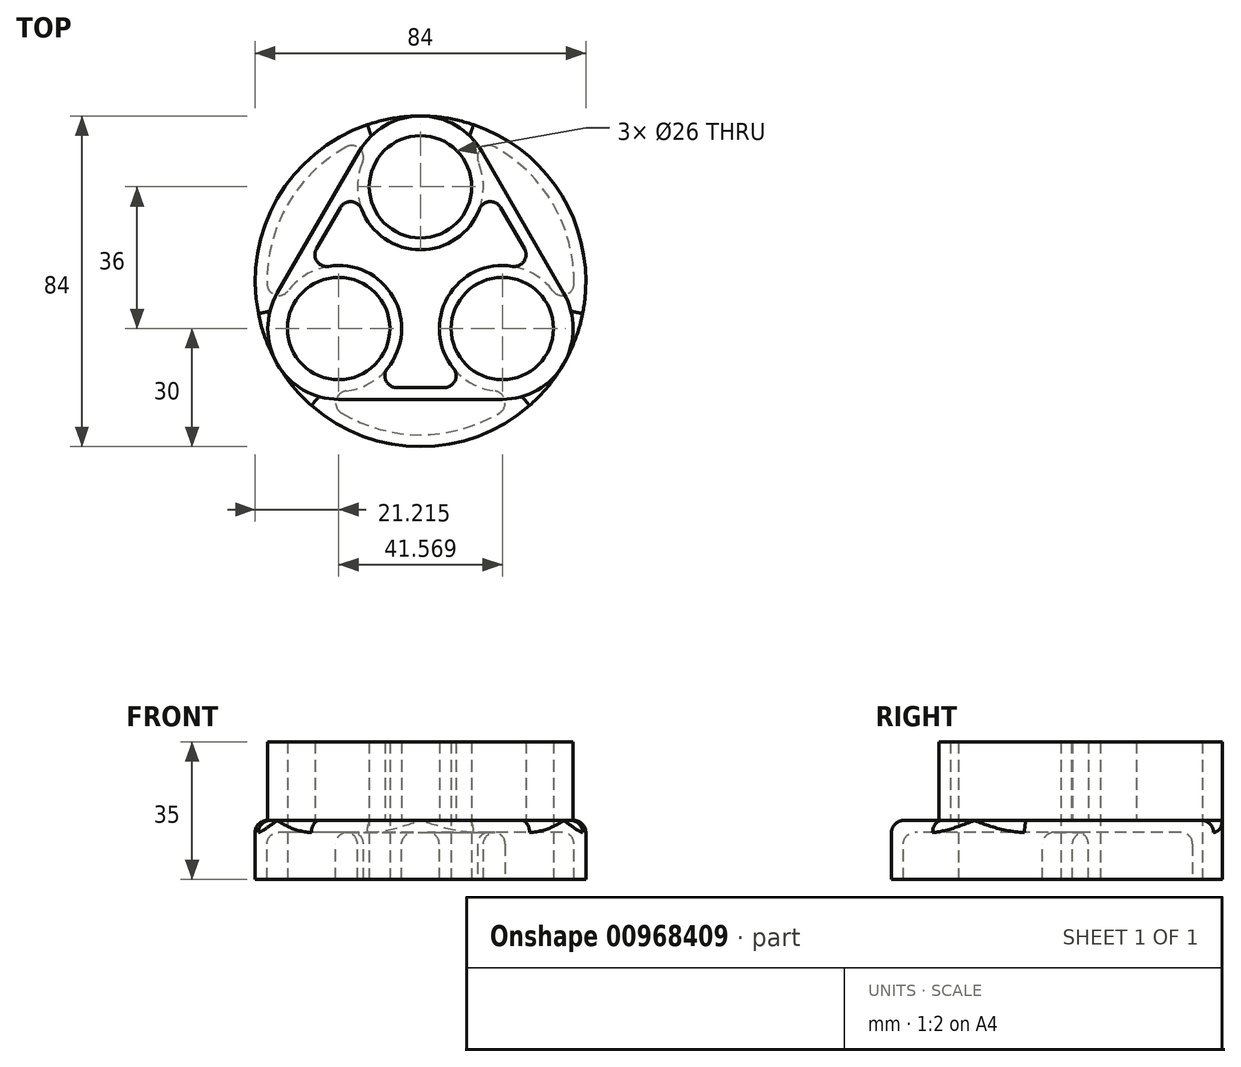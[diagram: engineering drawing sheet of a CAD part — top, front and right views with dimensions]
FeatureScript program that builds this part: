
annotation { "Feature Type Name" : "Feature", "Feature Type Description" : "" }
export const myFeature = defineFeature(function(context is Context, id is Id, definition is map)
    precondition{}
    {
        {
            var Q0;
            Q0=qCreatedBy(makeId("Top.planeOp"),FACE);
            var sketch = newSketch(context, id + "F0", { "sketchPlane" : qUnion([Q0])});
            skCircle(sketch, "E0", {"center": v(0, 0) * mm, "radius": 42 * mm, "construction": true});
            skCircle(sketch, "E1", {"center": v(0, 24) * mm, "radius": 13 * mm});
            skLineSegment(sketch, "E2", {"start": v(0, 0) * mm, "end": v(-20.78, -12) * mm, "construction": true});
            skLineSegment(sketch, "E3", {"start": v(0, 0) * mm, "end": v(20.78, -12) * mm, "construction": true});
            skCircle(sketch, "E4", {"center": v(-20.78, -12) * mm, "radius": 13 * mm});
            skCircle(sketch, "E5", {"center": v(20.78, -12) * mm, "radius": 13 * mm});
            skCircle(sketch, "E6", {"center": v(0, 0) * mm, "radius": 24 * mm, "construction": true});
            skArc(sketch, "E7", {"start": v(-15.59, 33) * mm, "mid": v(0, 42) * mm, "end": v(15.59, 33) * mm});
            skArc(sketch, "E8", {"start": v(-36.37, -3) * mm, "mid": v(-36.37, -21) * mm, "end": v(-20.78, -30) * mm});
            skArc(sketch, "E9", {"start": v(36.37, -3) * mm, "mid": v(36.37, -21) * mm, "end": v(20.78, -30) * mm});
            skLineSegment(sketch, "E10", {"start": v(-15.59, 33) * mm, "end": v(-36.37, -3) * mm});
            skLineSegment(sketch, "E11", {"start": v(15.59, 33) * mm, "end": v(36.37, -3) * mm});
            skLineSegment(sketch, "E12", {"start": v(-20.78, -30) * mm, "end": v(20.78, -30) * mm});
            skArc(sketch, "E13", {"start": v(-14.95, 18.3) * mm, "mid": v(0, 8) * mm, "end": v(14.95, 18.3) * mm});
            skArc(sketch, "E14", {"start": v(8.38, -22.1) * mm, "mid": v(6.93, -4) * mm, "end": v(23.33, 3.8) * mm});
            skArc(sketch, "E15", {"start": v(-23.33, 3.8) * mm, "mid": v(-6.93, -4) * mm, "end": v(-8.38, -22.1) * mm});
            skLineSegment(sketch, "E16", {"start": v(-6.05, -27) * mm, "end": v(6.05, -27) * mm});
            skLineSegment(sketch, "E17", {"start": v(20.36, 18.74) * mm, "end": v(26.4, 8.26) * mm});
            skLineSegment(sketch, "E18.0", {"start": v(-20.36, 18.74) * mm, "end": v(-26.4, 8.26) * mm});
            skPoint(sketch, "E19.visualSharp", {"position": v(-15.77, 26.68) * mm});
            skArc(sketch, "E19.filletArc", {"start": v(-14.95, 18.3) * mm, "mid": v(-17.52, 20.23) * mm, "end": v(-20.36, 18.74) * mm});
            skPoint(sketch, "E20.visualSharp", {"position": v(15.77, 26.68) * mm});
            skArc(sketch, "E20.filletArc", {"start": v(20.36, 18.74) * mm, "mid": v(17.52, 20.23) * mm, "end": v(14.95, 18.3) * mm});
            skPoint(sketch, "E21.visualSharp", {"position": v(31, 0.32) * mm});
            skArc(sketch, "E21.filletArc", {"start": v(23.33, 3.8) * mm, "mid": v(26.28, 5.05) * mm, "end": v(26.4, 8.26) * mm});
            skPoint(sketch, "E22.visualSharp", {"position": v(-31, 0.32) * mm});
            skArc(sketch, "E22.filletArc", {"start": v(-26.4, 8.26) * mm, "mid": v(-26.28, 5.05) * mm, "end": v(-23.33, 3.8) * mm});
            skPoint(sketch, "E23.visualSharp", {"position": v(15.22, -27) * mm});
            skArc(sketch, "E23.filletArc", {"start": v(6.05, -27) * mm, "mid": v(8.76, -25.29) * mm, "end": v(8.38, -22.1) * mm});
            skPoint(sketch, "E24.visualSharp", {"position": v(-15.22, -27) * mm});
            skArc(sketch, "E24.filletArc", {"start": v(-8.38, -22.1) * mm, "mid": v(-8.76, -25.29) * mm, "end": v(-6.05, -27) * mm});
            skSolve(sketch);
        }
        {
            var Q0;
            Q0=qCreatedBy(makeId("Top.planeOp"),FACE);
            var sketch = newSketch(context, id + "F1", { "sketchPlane" : qUnion([Q0])});
            skCircle(sketch, "E25.0", {"center": v(0, 0) * mm, "radius": 42 * mm});
            skCircle(sketch, "E26.0", {"center": v(0, 24) * mm, "radius": 13 * mm});
            skCircle(sketch, "E26.1", {"center": v(20.78, -12) * mm, "radius": 13 * mm});
            skCircle(sketch, "E26.2", {"center": v(-20.78, -12) * mm, "radius": 13 * mm});
            skCircle(sketch, "E27.0", {"center": v(0, 24) * mm, "radius": 16 * mm});
            skCircle(sketch, "E28.0", {"center": v(20.78, -12) * mm, "radius": 16 * mm});
            skCircle(sketch, "E29.0", {"center": v(-20.78, -12) * mm, "radius": 16 * mm});
            skSolve(sketch);
        }
        {
            var Q0;
            Q0=qSketchRegion(id+"F1",true);
            var Q1;
            Q1=makeQuery(id+"F1.imprint","IMPRINT",FACE,{"disambiguationData":[TD([[makeQuery(id+"F1.imprint","IMPRINT",EDGE,{"derivedFrom":sQuery(id+"F1.wireOp",EDGE,"E26.2")}),-1.0]])]});
            var Q2;
            Q2=makeQuery(id+"F1.imprint","IMPRINT",FACE,{"disambiguationData":[TD([[makeQuery(id+"F1.imprint","IMPRINT",EDGE,{"derivedFrom":sQuery(id+"F1.wireOp",EDGE,"E26.2")}),1.0]])]});
            var Q3;
            Q3=makeQuery(id+"F1.imprint","IMPRINT",FACE,{"disambiguationData":[TD([[makeQuery(id+"F1.imprint","IMPRINT",EDGE,{"derivedFrom":sQuery(id+"F1.wireOp",EDGE,"E26.0")}),-1.0]])]});
            var Q4;
            Q4=makeQuery(id+"F1.imprint","IMPRINT",FACE,{"disambiguationData":[TD([[makeQuery(id+"F1.imprint","IMPRINT",EDGE,{"derivedFrom":sQuery(id+"F1.wireOp",EDGE,"E26.0")}),1.0]])]});
            var Q5;
            Q5=makeQuery(id+"F1.imprint","IMPRINT",FACE,{"disambiguationData":[TD([[makeQuery(id+"F1.imprint","IMPRINT",EDGE,{"derivedFrom":sQuery(id+"F1.wireOp",EDGE,"E26.1")}),-1.0]])]});
            var Q6;
            Q6=makeQuery(id+"F1.imprint","IMPRINT",FACE,{"disambiguationData":[TD([[makeQuery(id+"F1.imprint","IMPRINT",EDGE,{"derivedFrom":sQuery(id+"F1.wireOp",EDGE,"E26.1")}),1.0]])]});
            extrude(context, id + "F2", {"entities" : qUnion([Q0, Q1, Q2, Q3, Q4, Q5, Q6]), "oppositeDirection" : true, "depth" : 15 * mm, "offsetDistance" : 25 * mm});
        }
        {
            var Q0;
            Q0=makeQuery(id+"F2.opExtrude","CAP_FACE",FACE,{"disambiguationData":[OSD([sQuery(id+"F1.wireOp",EDGE,"E25.0")])],"isStart":false});
            shell(context, id + "F3", {"entities" : qUnion([Q0]), "thickness" : 3 * mm});
        }
        {
            var Q0;
            Q0=makeQuery(id+"F0.imprint","IMPRINT",FACE,{"disambiguationData":[TD([[makeQuery(id+"F0.imprint","IMPRINT",EDGE,{"derivedFrom":sQuery(id+"F0.wireOp",EDGE,"E1")}),-1.0]])]});
            extrude(context, id + "F4", {"entities" : qUnion([Q0]), "operationType" : NewBodyOperationType.ADD, "depth" : 20 * mm, "offsetDistance" : 25 * mm});
        }
        {
            var Q0;
            Q0=makeQuery(id+"F0.imprint","IMPRINT",FACE,{"disambiguationData":[TD([[makeQuery(id+"F0.imprint","IMPRINT",EDGE,{"derivedFrom":sQuery(id+"F0.wireOp",EDGE,"E1")}),1.0]])]});
            var Q1;
            Q1=makeQuery(id+"F0.imprint","IMPRINT",FACE,{"disambiguationData":[TD([[makeQuery(id+"F0.imprint","IMPRINT",EDGE,{"derivedFrom":sQuery(id+"F0.wireOp",EDGE,"E4")}),1.0]])]});
            var Q2;
            Q2=makeQuery(id+"F0.imprint","IMPRINT",FACE,{"disambiguationData":[TD([[makeQuery(id+"F0.imprint","IMPRINT",EDGE,{"derivedFrom":sQuery(id+"F0.wireOp",EDGE,"E5")}),1.0]])]});
            extrude(context, id + "F5", {"entities" : qUnion([Q0, Q1, Q2]), "operationType" : NewBodyOperationType.REMOVE, "endBound" : BoundingType.THROUGH_ALL, "oppositeDirection" : true, "depth" : 25 * mm, "offsetDistance" : 25 * mm});
        }
        {
            var Q0;
            Q0=makeQuery(id+"F1.imprint","IMPRINT",FACE,{"disambiguationData":[TD([[makeQuery(id+"F1.imprint","IMPRINT",EDGE,{"derivedFrom":sQuery(id+"F1.wireOp",EDGE,"E26.0")}),-1.0]])]});
            var Q1;
            Q1=makeQuery(id+"F1.imprint","IMPRINT",FACE,{"disambiguationData":[TD([[makeQuery(id+"F1.imprint","IMPRINT",EDGE,{"derivedFrom":sQuery(id+"F1.wireOp",EDGE,"E26.1")}),-1.0]])]});
            var Q2;
            Q2=makeQuery(id+"F1.imprint","IMPRINT",FACE,{"disambiguationData":[TD([[makeQuery(id+"F1.imprint","IMPRINT",EDGE,{"derivedFrom":sQuery(id+"F1.wireOp",EDGE,"E26.2")}),-1.0]])]});
            var Q3;
            Q3=makeQuery(id+"F2.opExtrude","CAP_FACE",FACE,{"disambiguationData":[OSD([sQuery(id+"F1.wireOp",EDGE,"E25.0")])],"isStart":false});
            extrude(context, id + "F6", {"entities" : qUnion([Q0, Q1, Q2]), "operationType" : NewBodyOperationType.ADD, "endBound" : BoundingType.UP_TO_SURFACE, "oppositeDirection" : true, "depth" : 25 * mm, "endBoundEntityFace" : qUnion([Q3]), "offsetDistance" : 25 * mm});
        }
        {
            var Q0;
            Q0=makeQuery(id+"F4.opExtrude","CAP_EDGE",EDGE,{"disambiguationData":[OSD([sQuery(id+"F0.wireOp",EDGE,"E10")])],"isStart":true});
            var Q1;
            Q1=makeQuery(id+"F4.opExtrude","CAP_EDGE",EDGE,{"disambiguationData":[OSD([sQuery(id+"F0.wireOp",EDGE,"E16")])],"isStart":true});
            var Q2;
            {var subQ0=sQuery(id+"F1.wireOp",EDGE,"E25.0");Q2=makeQuery(id+"F6.boolean.opBoolean","INTERSECT",EDGE,{"disambiguationData":[OD(0.0)],"derivedFrom":[makeQuery(id+"F3.opShell","OFFSET_FACE",FACE,{"disambiguationData":[OSD([subQ0]),TDD([makeQuery(id+"F2.opExtrude","SWEPT_FACE",FACE,{"disambiguationData":[OSD([subQ0])]})])]}),makeQuery(id+"F6.opExtrude","SWEPT_FACE",FACE,{"disambiguationData":[OSD([sQuery(id+"F1.wireOp",EDGE,"E29.0")])]})]});}
            var Q3;
            {var subQ0=sQuery(id+"F1.wireOp",EDGE,"E25.0");Q3=makeQuery(id+"F6.boolean.opBoolean","INTERSECT",EDGE,{"disambiguationData":[OD(1.0)],"derivedFrom":[makeQuery(id+"F3.opShell","OFFSET_FACE",FACE,{"disambiguationData":[OSD([subQ0]),TDD([makeQuery(id+"F2.opExtrude","SWEPT_FACE",FACE,{"disambiguationData":[OSD([subQ0])]})])]}),makeQuery(id+"F6.opExtrude","SWEPT_FACE",FACE,{"disambiguationData":[OSD([sQuery(id+"F1.wireOp",EDGE,"E27.0")])]})]});}
            var Q4;
            {var subQ0=sQuery(id+"F1.wireOp",EDGE,"E25.0");Q4=makeQuery(id+"F6.boolean.opBoolean","INTERSECT",EDGE,{"disambiguationData":[OD(1.0)],"derivedFrom":[makeQuery(id+"F3.opShell","OFFSET_FACE",FACE,{"disambiguationData":[OSD([subQ0]),TDD([makeQuery(id+"F2.opExtrude","SWEPT_FACE",FACE,{"disambiguationData":[OSD([subQ0])]})])]}),makeQuery(id+"F6.opExtrude","SWEPT_FACE",FACE,{"disambiguationData":[OSD([sQuery(id+"F1.wireOp",EDGE,"E28.0")])]})]});}
            var Q5;
            {var subQ0=sQuery(id+"F1.wireOp",EDGE,"E25.0");Q5=makeQuery(id+"F6.boolean.opBoolean","INTERSECT",EDGE,{"disambiguationData":[OD(0.0)],"derivedFrom":[makeQuery(id+"F3.opShell","OFFSET_FACE",FACE,{"disambiguationData":[OSD([subQ0]),TDD([makeQuery(id+"F2.opExtrude","SWEPT_FACE",FACE,{"disambiguationData":[OSD([subQ0])]})])]}),makeQuery(id+"F6.opExtrude","SWEPT_FACE",FACE,{"disambiguationData":[OSD([sQuery(id+"F1.wireOp",EDGE,"E28.0")])]})]});}
            var Q6;
            {var subQ0=sQuery(id+"F1.wireOp",EDGE,"E25.0");Q6=makeQuery(id+"F6.boolean.opBoolean","INTERSECT",EDGE,{"disambiguationData":[OD(0.0)],"derivedFrom":[makeQuery(id+"F3.opShell","OFFSET_FACE",FACE,{"disambiguationData":[OSD([subQ0]),TDD([makeQuery(id+"F2.opExtrude","SWEPT_FACE",FACE,{"disambiguationData":[OSD([subQ0])]})])]}),makeQuery(id+"F6.opExtrude","SWEPT_FACE",FACE,{"disambiguationData":[OSD([sQuery(id+"F1.wireOp",EDGE,"E27.0")])]})]});}
            var Q7;
            {var subQ0=sQuery(id+"F1.wireOp",EDGE,"E25.0");Q7=makeQuery(id+"F6.boolean.opBoolean","INTERSECT",EDGE,{"disambiguationData":[OD(1.0)],"derivedFrom":[makeQuery(id+"F3.opShell","OFFSET_FACE",FACE,{"disambiguationData":[OSD([subQ0]),TDD([makeQuery(id+"F2.opExtrude","SWEPT_FACE",FACE,{"disambiguationData":[OSD([subQ0])]})])]}),makeQuery(id+"F6.opExtrude","SWEPT_FACE",FACE,{"disambiguationData":[OSD([sQuery(id+"F1.wireOp",EDGE,"E29.0")])]})]});}
            fillet(context, id + "F7", {"entities" : qUnion([Q0, Q1, Q2, Q3, Q4, Q5, Q6, Q7]), "tangentPropagation" : true, "radius" : 3 * mm, "defaultsChanged" : false, "vertexSettings" : [], "allowEdgeOverflow" : false});
        }
        {
            var Q0;
            {var subQ0=sQuery(id+"F1.wireOp",EDGE,"E25.0");Q0=makeQuery(id+"F6.boolean.opBoolean","SPLIT",EDGE,{"disambiguationData":[TD([makeQuery(id+"F3.opShell","OFFSET_FACE",FACE,{"disambiguationData":[OSD([subQ0]),TDD([makeQuery(id+"F2.opExtrude","SWEPT_FACE",FACE,{"disambiguationData":[OSD([subQ0])]})])]}),makeQuery(id+"F3.opShell","OFFSET_FACE",FACE,{"disambiguationData":[OSD([subQ0]),TDD([makeQuery(id+"F2.opExtrude","CAP_FACE",FACE,{"disambiguationData":[OSD([subQ0])],"isStart":true})])]}),makeQuery(id+"F6.opExtrude","SWEPT_FACE",FACE,{"disambiguationData":[OSD([sQuery(id+"F1.wireOp",EDGE,"E27.0")])]}),makeQuery(id+"F6.opExtrude","SWEPT_FACE",FACE,{"disambiguationData":[OSD([sQuery(id+"F1.wireOp",EDGE,"E29.0")])]})])],"derivedFrom":makeQuery(id+"F3.opShell","OFFSET_EDGE",EDGE,{"disambiguationData":[OSD([subQ0]),TDD([makeQuery(id+"F2.opExtrude","CAP_EDGE",EDGE,{"disambiguationData":[OSD([subQ0])],"isStart":true})])]})});}
            var Q1;
            {var subQ0=sQuery(id+"F1.wireOp",EDGE,"E25.0");Q1=makeQuery(id+"F4.boolean.opBoolean","SPLIT",EDGE,{"disambiguationData":[TD([makeQuery(id+"F2.opExtrude","SWEPT_FACE",FACE,{"disambiguationData":[OSD([subQ0])]}),makeQuery(id+"F2.opExtrude","CAP_FACE",FACE,{"disambiguationData":[OSD([subQ0])],"isStart":true}),makeQuery(id+"F4.opExtrude","SWEPT_FACE",FACE,{"disambiguationData":[OSD([sQuery(id+"F0.wireOp",EDGE,"E8")])]}),makeQuery(id+"F4.opExtrude","SWEPT_FACE",FACE,{"disambiguationData":[OSD([sQuery(id+"F0.wireOp",EDGE,"E9")])]})])],"derivedFrom":makeQuery(id+"F2.opExtrude","CAP_EDGE",EDGE,{"disambiguationData":[OSD([subQ0])],"isStart":true})});}
            var Q2;
            {var subQ0=sQuery(id+"F1.wireOp",EDGE,"E25.0");Q2=makeQuery(id+"F4.boolean.opBoolean","SPLIT",EDGE,{"disambiguationData":[TD([makeQuery(id+"F2.opExtrude","SWEPT_FACE",FACE,{"disambiguationData":[OSD([subQ0])]}),makeQuery(id+"F2.opExtrude","CAP_FACE",FACE,{"disambiguationData":[OSD([subQ0])],"isStart":true}),makeQuery(id+"F4.opExtrude","SWEPT_FACE",FACE,{"disambiguationData":[OSD([sQuery(id+"F0.wireOp",EDGE,"E7")])]}),makeQuery(id+"F4.opExtrude","SWEPT_FACE",FACE,{"disambiguationData":[OSD([sQuery(id+"F0.wireOp",EDGE,"E8")])]})])],"derivedFrom":makeQuery(id+"F2.opExtrude","CAP_EDGE",EDGE,{"disambiguationData":[OSD([subQ0])],"isStart":true})});}
            var Q3;
            {var subQ0=sQuery(id+"F1.wireOp",EDGE,"E25.0");Q3=makeQuery(id+"F4.boolean.opBoolean","SPLIT",EDGE,{"disambiguationData":[TD([makeQuery(id+"F2.opExtrude","SWEPT_FACE",FACE,{"disambiguationData":[OSD([subQ0])]}),makeQuery(id+"F2.opExtrude","CAP_FACE",FACE,{"disambiguationData":[OSD([subQ0])],"isStart":true}),makeQuery(id+"F4.opExtrude","SWEPT_FACE",FACE,{"disambiguationData":[OSD([sQuery(id+"F0.wireOp",EDGE,"E7")])]}),makeQuery(id+"F4.opExtrude","SWEPT_FACE",FACE,{"disambiguationData":[OSD([sQuery(id+"F0.wireOp",EDGE,"E9")])]})])],"derivedFrom":makeQuery(id+"F2.opExtrude","CAP_EDGE",EDGE,{"disambiguationData":[OSD([subQ0])],"isStart":true})});}
            fillet(context, id + "F8", {"entities" : qUnion([Q0, Q1, Q2, Q3]), "tangentPropagation" : true, "radius" : 3 * mm, "defaultsChanged" : false, "vertexSettings" : [], "allowEdgeOverflow" : false});
        }
    });
